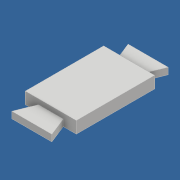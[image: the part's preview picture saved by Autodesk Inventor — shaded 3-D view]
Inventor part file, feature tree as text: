
AUTODESK INVENTOR PART (.ipt)
format: ipt  version: 2017 (Build 210142000, 142)  size: 108,032 bytes
history: native  units: mm
features: extrude x3, sketch x3, other x1
ambient origin geometry x8: Origin, YZ Plane, XZ Plane, XY Plane, X Axis, Y Axis, Z Axis, Center Point
bodies: Body1 (feature_tree)
feature tree (7):
  other  "ソリッド1"
  extrude  "押し出し1"  Depth=7.2mm
  extrude  "押し出し2"  Depth=11.5mm
  extrude  "押し出し3"  Depth=45.0mm
  sketch  "スケッチ1"
  sketch  "スケッチ2"
  sketch  "スケッチ3"
